# Revit family: Faucet-DXV-Modulus-D35120802_Series
name_source: partatom
category: Plumbing Fixtures
units: mm (PartAtom-declared; Revit-internal decimal feet)

## family parameters
Always vertical = No
Cut with Voids When Loaded = Yes
OmniClass Number = 23.45.55.17
OmniClass Title = Mixing Faucets
Part Type = Normal
Room Calculation Point = No
Round Connector Dimension = Use Radius
Shared = Yes
Work Plane-Based = Yes

## types (4) — shared parameters
ADA Compliant = Yes
ASME A112.18.1/CSA B125.1 = Yes
Assembly Code = D2020300
CEC Compliant = Yes
CW Connection = Yes
CWFU = 1.5
CalGreen Compliant = Yes
Cold Water Connection Radius = 1/4"
Cold Water Diameter = 1/2"
Default Elevation = 0"
Description = DXV Modulus Widespread Lavatory Faucet
EPA WaterSense® Certified = Yes
Flow Rate = 1.2 gpm (4.5 L/min)
HW Connection = Yes
HWFU = 1.5
Height = 3 1/8"
Hot Water Connection Diameter = 1/2"
Hot Water Connection Radius = 1/4"
Installation Instruction Link = https://dxv01.blob.core.windows.net
Installation Type = Deck Mounted
Length = 14 1/2"
Manufacturer = DXV
NSF 61/Section 9 = Yes
Price = Prices may vary. Please consult Manufacturer Rep for most up-to-date price list.
Product Documentation Link = https://dxv01.blob.core.windows.net
Product Page URL = https://www.dxv.com
Revised Date = 04/05/2022
URL = https://www.dxv.com
Vent Connection = No
WFU = 2
Waste Connection = No
Width = 5 1/8"

## per-type parameters (varying)
| type | Finish | Finish 2 | Material |
| D35120802.100 | Brass-DXV-100-Polished Chrome | Brass-DXV-144-Brushed Nickel | Brass-DXV-100-Polished Chrome |
| D35120802.144 | Brass-DXV-144-Brushed Nickel | Brass-DXV-150-Platinum Nickel | Brass-DXV-144-Brushed Nickel |
| D35120802.150 | Brass-DXV-150-Platinum Nickel | Brass-DXV-144-Brushed Nickel | Brass-DXV-150-Platinum Nickel |
| D35120802.243 | Brass-DXV-243-Matte Black | Brass-DXV-243-Matte Black | Brass-DXV-243-Matte Black |

note: column(s) folded — value = type name in every type: Model

## geometry (parser evidence)
native form markers: Sweep x2
no freeform markers — native parametric forms only
